# Revit family: 3469A_NX_Audio_Visual_Interface_Module
name_source: partatom
category: Communication Devices
units: mm (PartAtom-declared; Revit-internal decimal feet)

## family parameters
Cut with Voids When Loaded = No
Host = Face
Maintain Annotation Orientation = No
OmniClass Number = 23.85.80.11.27
OmniClass Title = Lighting Controls
Part Type = Normal
Room Calculation Point = No
Round Connector Dimension = Use Diameter
Shared = Yes

## types (1)
- 3469A_NX_Audio_Visual_Interface_Module
    Apparent Load = 0 VA
    Assembly Code = D5090
    Black Material = Paint -  Black Matte Textured
    Default Elevation = 48 "
    Description = The NX Audio Visual Interface Module allows third party systems
to digitally interface with an NX distributed lighting control
system
    Features = • Mounts to standard 4 11/16” junction box, Raco #257 or similar
(not supplied)
• Connects to and is powered by NX SmartPORT™ with CAT5 cable
• Class 2 device, self powered from SmartPORT connection
• DB9 connector for RS232 serial communication
• Simple ASCII based command set
    Green Element = Plastic -  Green
    Manufacturer = NX Lighting Controls
    Model = Audio Visual Interface
    Steel = Metal-Galvanized_Steel
    Type Comments = Audio Visual Interface
    URL = https://www.currentlighting.com
    Voltage = 24 V
    Warranty = 5-Years Warranty
    White Element = Glass, White, High Luminance

## geometry (parser evidence)
native form markers: Sweep x2
no freeform markers — native parametric forms only
